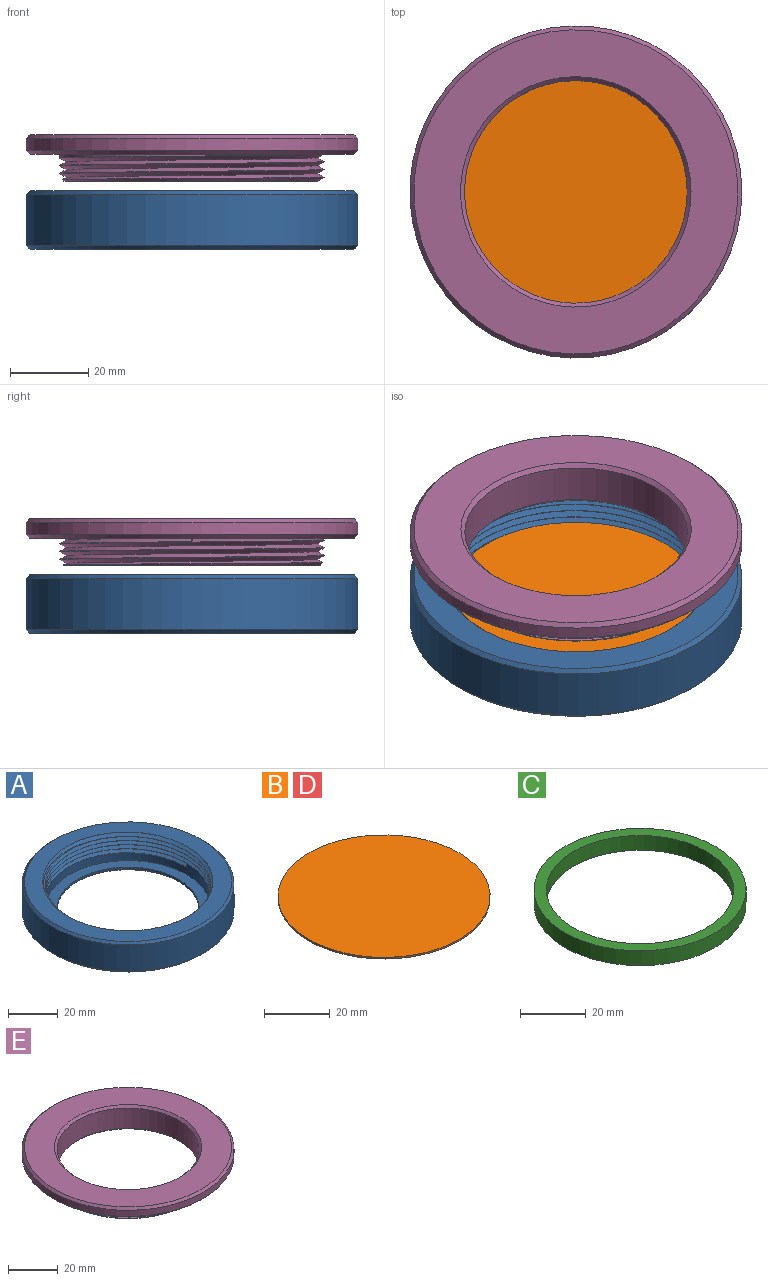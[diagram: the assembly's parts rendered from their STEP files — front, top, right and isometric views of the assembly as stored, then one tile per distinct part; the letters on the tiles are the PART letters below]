
ASSEMBLY  parts=5 mates=4
PART A: 17 faces, bbox 85.6x85.6x16.8 mm
  f0: cylinder r=33.05mm len=66.1mm, axis (0,0,1), area 955.2mm2, adj f4,f8,f14,f16
  f1: cylinder r=33.05mm len=33.05mm, axis (0,0,1), area 4.7mm2, adj f2,f13,f15,f16
  f2: cylinder r=33.05mm len=66.1mm, axis (0,0,1), area 20.7mm2, adj f1,f3,f15,f16
  f3: cylinder r=33.05mm len=66.1mm, axis (0,0,1), area 20.7mm2, adj f2,f4,f15,f16
  f4: cylinder r=33.05mm len=66.1mm, axis (0,0,1), area 20.6mm2, adj f0,f3,f15,f16
  f5: cylinder r=42.5mm len=85mm, axis (0,0,-1), area 3471.5mm2, adj f10,f11
  f6: plane 83.6x83.6mm, normal (0,0,1), area 1742.3mm2, adj f10,f13,f15,f16
  f7: plane 83x83mm, normal (0,0,-1), area 2676.6mm2, adj f11,f12
  f8: plane 66.1x66.1mm, normal (0,0,1), area 879.8mm2, adj f0,f9
  f9: cylinder r=28.5mm len=57mm, axis (0,0,1), area 179.1mm2, adj f8,f12
  f10: cone r=41.5mm half-angle=45deg, axis (0,0,-1), area 373.2mm2, adj f5,f6
  f11: cone r=42.5mm half-angle=45deg, axis (0,0,1), area 373.2mm2, adj f5,f7
  f12: cone r=29.5mm half-angle=45deg, axis (0,0,-1), area 257.7mm2, adj f7,f9
  f13: cone r=33.05mm half-angle=45deg, axis (0,0,1), area 101.4mm2, adj f1,f6,f15,f16
  f14: plane 1.9x1.65mm, normal (0,1,0), area 1.6mm2, adj f0,f15,f16
  f15: bspline ~80.13x69.39mm, area 1551.8mm2, adj f1,f2,f3,f4,f6,f13,f14,f16
  f16: bspline ~80.13x69.39mm, area 1743.7mm2, adj f0,f1,f2,f3,f4,f6,f13,f14
PART B: 3 faces, bbox 64.5x64.5x0.6 mm
  f0: cylinder r=32.25mm len=64.5mm, axis (0,0,-1), area 121.6mm2, adj f1,f2
  f1: plane 64.5x64.5mm, normal (0,0,1), area 3267.5mm2, adj f0
  f2: plane 64.5x64.5mm, normal (0,0,-1), area 3267.5mm2, adj f0
PART C: 4 faces, bbox 64.5x64.5x5.5 mm
  f0: cylinder r=28.5mm len=57mm, axis (0,0,-1), area 984.9mm2, adj f2,f3
  f1: cylinder r=32.25mm len=64.5mm, axis (0,0,-1), area 1114.5mm2, adj f2,f3
  f2: plane 64.5x64.5mm, normal (0,0,1), area 715.7mm2, adj f0,f1
  f3: plane 64.5x64.5mm, normal (0,0,-1), area 715.7mm2, adj f0,f1
PART D: same geometry as B
PART E: 15 faces, bbox 85.7x85.7x13.6 mm
  f0: plane 66.4x65.85mm, normal (0,0,-1), area 631.6mm2, adj f6,f8,f9,f12
  f1: cylinder r=33.85mm len=67.7mm, axis (0,0,-1), area 104.2mm2, adj f4,f8,f9,f10,f12
  f2: cylinder r=42.5mm len=85mm, axis (0,0,-1), area 801.1mm2, adj f13,f14
  f3: plane 83x83mm, normal (0,0,1), area 2676.6mm2, adj f7,f13
  f4: plane 83x83mm, normal (0,0,-1), area 1810.9mm2, adj f1,f11,f14
  f5: cylinder r=28.5mm len=57mm, axis (0,0,1), area 1772.8mm2, adj f6,f7
  f6: cone r=29.5mm half-angle=45deg, axis (0,0,-1), area 257.7mm2, adj f0,f5
  f7: cone r=28.5mm half-angle=45deg, axis (0,0,1), area 257.7mm2, adj f3,f5
  f8: bspline ~78.17x67.7mm, area 1215.2mm2, adj f0,f1,f9,f10,f12
  f9: bspline ~78.17x67.7mm, area 1401.4mm2, adj f0,f1,f8,f10,f11,f12
  f10: plane 1.9x1.65mm, normal (0,1,0), area 1.6mm2, adj f1,f8,f9,f11
  f11: cylinder r=33.85mm len=67.7mm, axis (0,0,1), area 53mm2, adj f4,f9,f10
  f12: cone r=33.85mm half-angle=45deg, axis (0,0,1), area 100mm2, adj f0,f1,f8,f9
  f13: cone r=41.5mm half-angle=45deg, axis (0,0,-1), area 373.2mm2, adj f2,f3
  f14: cone r=42.5mm half-angle=45deg, axis (0,0,1), area 373.2mm2, adj f2,f4
PLACE A t=(8.68,-7.07,-27.39)mm fixed
PLACE B t=(8.68,-7.07,-21.3)mm
PLACE C t=(8.68,-7.07,-27.4)mm
PLACE D t=(8.68,-7.07,-27.4)mm
PLACE E t=(8.68,-7.07,-18.01)mm
MATE revolute C.f1 <-> B.f0  axis (0,0,1) through (8.68,-7.07,-19.3)mm
MATE revolute C.f1 <-> D.f0  axis (0,0,-1) through (8.68,-7.07,-24.8)mm
MATE slider A.f5 <-> E.f2  axis (0,0,1) through (8.68,-7.07,-12.39)mm
MATE slider D.f0 <-> A.f9  axis (0,0,-1) through (8.68,-7.07,-25.4)mm
